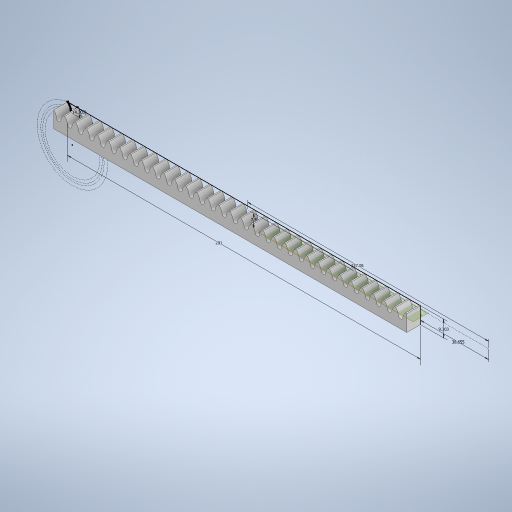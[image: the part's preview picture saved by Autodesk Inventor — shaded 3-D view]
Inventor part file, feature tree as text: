
AUTODESK INVENTOR PART (.ipt)
format: ipt  version: 2023 (Build 270158000, 158)  size: 371,200 bytes
history: native  units: mm
features: extrude x2, other x1, sketch x1, pattern_linear x1, plane x1
ambient origin geometry x8: Origin, YZ Plane, XZ Plane, XY Plane, X Axis, Y Axis, Z Axis, Center Point
bodies: Body1 (feature_tree)
feature tree (6):
  other  "pinion"
  sketch  "Sketch1"  dims[d2=9.303mm d3=201.0mm d4=4.303311mm d5=7.82mm d6=0.0mm d7=0.0mm d8=0.0mm d9=320.0mm d11=6.28mm d12=137.050182mm d14=90.0deg d15=38.65503mm d16=7.499689mm]
  extrude  "Extrusion2"  Depth=201.0mm
  extrude  "Extrusion3"  Depth=4.303311mm
  pattern_linear  "Rectangular Pattern1"  Spacing1=7.82mm  [1 undecoded]
  plane  "Work Plane1"
note: 1 required parameter value undecoded (feature->parameter linkage not recoverable at this tier; creation-order binding heuristic only, values carry confidence <= 0.55)
